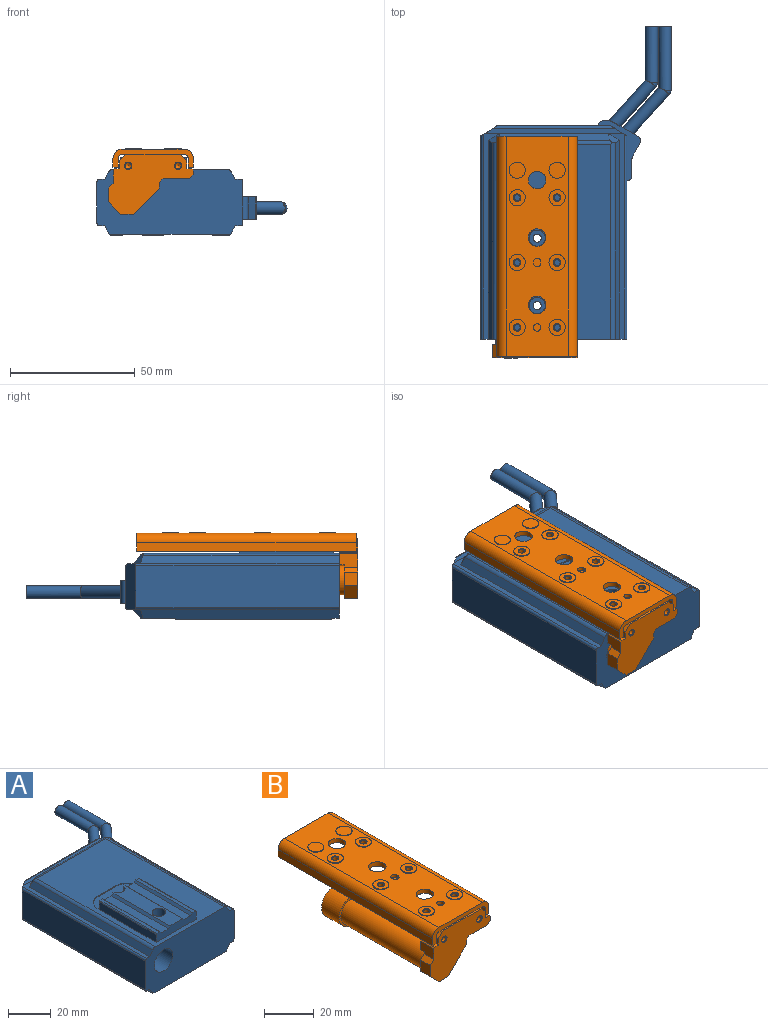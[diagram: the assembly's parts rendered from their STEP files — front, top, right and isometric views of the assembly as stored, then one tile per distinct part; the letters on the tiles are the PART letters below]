
ASSEMBLY  parts=2 mates=1
PART A: 108 faces, bbox 76.8x126.2x32.1 mm
  f0: plane 5x5mm, normal (0,1,0), area 19.6mm2, adj f3
  f1: plane 5x5mm, normal (0,1,0), area 19.6mm2, adj f4
  f2: revolved ~5x2.5mm, area 9.1mm2, adj f3,f8
  f3: cylinder r=2.5mm len=22.72mm, axis (0,1,0), area 353.2mm2, adj f0,f2,f8
  f4: cylinder r=2.5mm len=25.66mm, axis (0,-1,0), area 398.3mm2, adj f1,f5,f9
  f5: sphere r=2.5mm, area 11.9mm2, adj f4,f9
  f6: plane 6.5x6.5mm, normal (0,0,1), area 24.6mm2, adj f11,f13
  f7: plane 6.5x6.5mm, normal (0,0,1), area 24.6mm2, adj f10,f14
  f8: cylinder r=2.5mm len=20.28mm, axis (0.67,0.74,0), area 340.2mm2, adj f2,f3,f15,f17,f18,f19
  f9: cylinder r=2.5mm len=20.09mm, axis (-0.67,-0.74,0), area 340.4mm2, adj f4,f5,f19
  f10: cylinder r=3.25mm len=7.9mm, axis (0,0,1), area 161.3mm2, adj f7,f28
  f11: cylinder r=3.25mm len=7.9mm, axis (0,0,1), area 98.6mm2, adj f6,f28,f34,f35,f36
  f12: plane 14.2x14.2mm, normal (0,-1,0), area 158.4mm2, adj f38
  f13: cylinder r=1.65mm len=23.15mm, axis (0,0,1), area 240mm2, adj f6,f39
  f14: cylinder r=1.65mm len=23.15mm, axis (0,0,1), area 240mm2, adj f7,f40
  f15: cylinder r=2mm len=3.59mm, axis (0,0,-1), area 3.2mm2, adj f8,f17,f19,f44
  f16: cylinder r=2mm len=9mm, axis (0,0,-1), area 28.3mm2, adj f17,f43,f44,f45
  f17: plane 9.08x2.54mm, normal (0,1,0), area 21.9mm2, adj f8,f15,f16,f18,f44,f45
  f18: cylinder r=2mm len=3.59mm, axis (0,0,-1), area 3.2mm2, adj f8,f17,f19,f45
  f19: plane 10.72x9.22mm, normal (0.5,0.87,0), area 72.3mm2, adj f8,f9,f15,f18,f20,f44,f45
  f20: cylinder r=2mm len=9mm, axis (0,0,-1), area 28.3mm2, adj f19,f21,f44,f45
  f21: plane 9x5.07mm, normal (0.87,-0.5,0), area 52.7mm2, adj f20,f22,f44,f45
  f22: cylinder r=2mm len=9mm, axis (0,0,-1), area 9.4mm2, adj f21,f23,f44,f45
  f23: plane 9x6.86mm, normal (1,0,0), area 61.8mm2, adj f22,f44,f45,f46
  f24: plane 37.6x1.8mm, normal (0,0,1), area 67.7mm2, adj f25,f36,f37,f49
  f25: plane 37.6x1.1mm, normal (-0.71,0,0.71), area 58.5mm2, adj f24,f26,f36,f49
  f26: plane 37.6x4.6mm, normal (0,0,1), area 173mm2, adj f25,f27,f36,f49
  f27: plane 37.6x1.1mm, normal (0.71,0,0.71), area 58.5mm2, adj f26,f28,f36,f49
  f28: plane 37.6x8.2mm, normal (0,0,1), area 263.1mm2, adj f10,f11,f27,f29,f34,f36,f49
  f29: plane 37.6x1.1mm, normal (-0.71,0,0.71), area 58.5mm2, adj f28,f30,f34,f49
  f30: plane 37.6x4.6mm, normal (0,0,1), area 173mm2, adj f29,f31,f34,f49
  f31: plane 37.6x1.1mm, normal (0.71,0,0.71), area 58.5mm2, adj f30,f32,f34,f49
  f32: plane 37.6x1.8mm, normal (0,0,1), area 67.7mm2, adj f31,f33,f34,f49
  f33: cylinder r=0.5mm len=37.6mm, axis (0,-1,0), area 29.5mm2, adj f32,f34,f49,f50
  f34: plane 10.03x5.4mm, normal (0,1,0), area 47.8mm2, adj f11,f28,f29,f30,f31,f32,f33,f35
  f35: plane 26.4x8.2mm, normal (0,0,1), area 171.2mm2, adj f11,f34,f36,f51,f52,f53,f54,f55
  f36: plane 10.03x5.4mm, normal (0,1,0), area 47.8mm2, adj f11,f24,f25,f26,f27,f28,f35,f37
  f37: cylinder r=0.5mm len=37.6mm, axis (0,-1,0), area 29.5mm2, adj f24,f36,f49,f56
  f38: cylinder r=7.1mm len=42mm, axis (0,1,0), area 1873.6mm2, adj f12,f60
  f39: cone r=0mm half-angle=45deg, axis (0,0,-1), area 5.7mm2, adj f13,f62
  f40: cone r=0mm half-angle=45deg, axis (0,0,-1), area 5.7mm2, adj f14,f62
  f41: plane 55.15x2mm, normal (0,0,1), area 103.9mm2, adj f42,f47,f58,f64
  f42: cylinder r=1mm len=48.72mm, axis (-1,0,0), area 74mm2, adj f41,f43,f47,f64
  f43: plane 45.5x16.5mm, normal (0,1,0), area 705.8mm2, adj f16,f42,f44,f45,f47,f64,f65,f66
  f44: plane 24x16.97mm, normal (0,0,1), area 81mm2, adj f15,f16,f17,f19,f20,f21,f22,f23
  f45: plane 24x16.97mm, normal (0,0,-1), area 81mm2, adj f16,f17,f18,f19,f20,f21,f22,f23
  f46: cylinder r=2mm len=9mm, axis (0,0,-1), area 28.3mm2, adj f23,f44,f45,f69
  f47: plane 7.68x7.18mm, normal (0.53,0.85,0), area 52mm2, adj f41,f42,f43,f44,f58,f69,f70,f71
  f48: plane 4.87x4.18mm, normal (0.44,0.75,0.5), area 14.8mm2, adj f57,f58,f71,f72,f73
  f49: plane 26.4x4.9mm, normal (0,-1,0), area 116.7mm2, adj f24,f25,f26,f27,f28,f29,f30,f31
  f50: plane 37.6x4.4mm, normal (-1,0,0), area 165.4mm2, adj f33,f34,f49,f74
  f51: plane 0.7x0.5mm, normal (1,0,0), area 0.3mm2, adj f34,f35,f52,f74
  f52: cylinder r=7.5mm len=7.5mm, axis (0,0,1), area 5.9mm2, adj f35,f51,f53,f74
  f53: plane 11.4x0.5mm, normal (0,-1,0), area 5.7mm2, adj f35,f52,f54,f74
  f54: cylinder r=7.5mm len=7.5mm, axis (0,0,1), area 5.9mm2, adj f35,f53,f55,f74
  f55: plane 0.7x0.5mm, normal (-1,0,0), area 0.3mm2, adj f35,f36,f54,f74
  f56: plane 37.6x4.4mm, normal (1,0,0), area 165.4mm2, adj f36,f37,f49,f74
  f57: cylinder r=2mm len=46.85mm, axis (-1,0,0), area 80.7mm2, adj f48,f58,f59,f73,f74,f75
  f58: plane 55.56x3.43mm, normal (0,0.77,0.64), area 199.9mm2, adj f41,f47,f48,f57,f59,f64,f71,f77
  f59: plane 4.87x4.18mm, normal (-0.44,0.75,0.5), area 14.8mm2, adj f57,f58,f75,f76,f77
  f60: plane 14.2x14.2mm, normal (0,1,0), area 41.5mm2, adj f38,f81
  f61: plane 62.5x4.98mm, normal (0,0,-1), area 311.2mm2, adj f83,f84,f85,f86
  f62: plane 62.5x8.57mm, normal (0,0,-1), area 510.5mm2, adj f39,f40,f88,f89,f90,f91
  f63: plane 45.07x2.92mm, normal (0,0.74,-0.67), area 172.3mm2, adj f67,f82,f87,f92
  f64: plane 19.18x7.18mm, normal (-0.53,0.85,0), area 139.6mm2, adj f41,f42,f43,f58,f65,f77,f78,f79
  f65: cylinder r=1mm len=47.02mm, axis (-1,0,0), area 47mm2, adj f43,f64,f66,f93
  f66: plane 6.86x4.4mm, normal (0.53,0.85,0), area 18.7mm2, adj f43,f45,f65,f68,f69,f93
  f67: plane 42.9x0.42mm, normal (0,0.87,-0.5), area 20.7mm2, adj f63,f87,f92,f93
  f68: cylinder r=1mm len=82.08mm, axis (0,-1,0), area 128.4mm2, adj f66,f69,f93,f94
  f69: plane 81.46x16.5mm, normal (1,0,0), area 1182.4mm2, adj f44,f45,f46,f47,f66,f68,f70,f94
  f70: cylinder r=1mm len=82.08mm, axis (0,-1,0), area 128.4mm2, adj f47,f69,f71,f94
  f71: plane 82.38x6.59mm, normal (0,0,1), area 170.8mm2, adj f47,f48,f58,f70,f72,f94
  f72: plane 79.7x3mm, normal (0.87,0,0.5), area 274.4mm2, adj f48,f71,f73,f94
  f73: cylinder r=2mm len=78.74mm, axis (0,-1,0), area 164.7mm2, adj f48,f57,f72,f74,f94
  f74: plane 78.1x45.57mm, normal (0,0,1), area 2374.4mm2, adj f49,f50,f51,f52,f53,f54,f55,f56
  f75: cylinder r=2mm len=78.74mm, axis (0,-1,0), area 159.9mm2, adj f57,f59,f74,f76,f94
  f76: plane 79.7x3.05mm, normal (-0.87,0,0.5), area 279.1mm2, adj f59,f75,f77,f94
  f77: plane 82.38x6.59mm, normal (0,0,1), area 170.8mm2, adj f58,f59,f64,f76,f78,f94
  f78: cylinder r=1mm len=82.08mm, axis (0,-1,0), area 128.4mm2, adj f64,f77,f79,f94
  f79: plane 81.46x16.5mm, normal (-1,0,0), area 1344.1mm2, adj f64,f78,f80,f94
  f80: cylinder r=1mm len=82.08mm, axis (0,-1,0), area 128.4mm2, adj f64,f79,f93,f94
  f81: cylinder r=6.1mm len=12.5mm, axis (0,1,0), area 479.1mm2, adj f60,f94
  f82: cylinder r=2mm len=45.26mm, axis (-1,0,0), area 10.5mm2, adj f63,f87,f92,f95
  f83: plane 5.56x0.5mm, normal (0,-1,0), area 2.6mm2, adj f61,f84,f86,f95
  f84: plane 62.5x0.5mm, normal (0.87,0,-0.5), area 36.1mm2, adj f61,f83,f85,f95
  f85: plane 5.56x0.5mm, normal (0,1,0), area 2.6mm2, adj f61,f84,f86,f95
  f86: plane 79.7x4mm, normal (-0.87,0,-0.5), area 355.8mm2, adj f61,f83,f85,f87,f93,f94,f95
  f87: plane 4.88x3.97mm, normal (-0.44,0.75,-0.5), area 15.5mm2, adj f63,f67,f82,f86,f93,f95
  f88: plane 9.15x0.5mm, normal (0,1,0), area 4.4mm2, adj f62,f89,f91,f95
  f89: plane 62.5x0.5mm, normal (-0.87,0,-0.5), area 36.1mm2, adj f62,f88,f90,f95
  f90: plane 9.15x0.5mm, normal (0,-1,0), area 4.4mm2, adj f62,f89,f91,f95
  f91: plane 62.5x0.5mm, normal (0.87,0,-0.5), area 36.1mm2, adj f62,f88,f90,f95
  f92: plane 4.88x3.97mm, normal (0.44,0.75,-0.5), area 15.5mm2, adj f63,f67,f82,f93,f95,f98
  f93: plane 85.03x56.5mm, normal (0,0,-1), area 472.2mm2, adj f64,f65,f66,f67,f68,f80,f86,f87
  f94: plane 58.5x26mm, normal (0,-1,0), area 1341.5mm2, adj f68,f69,f70,f71,f72,f73,f74,f75
  f95: plane 79.47x48.46mm, normal (0,0,-1), area 2458.4mm2, adj f82,f83,f84,f85,f86,f87,f88,f89
  f96: plane 3x3mm, normal (0,0,-1), area 7.1mm2, adj f102
  f97: plane 7.56x0.5mm, normal (0,1,0), area 3.6mm2, adj f95,f98,f100,f105
  f98: plane 79.7x4mm, normal (0.87,0,-0.5), area 355.9mm2, adj f92,f93,f94,f95,f97,f99,f105
  f99: plane 7.56x0.5mm, normal (0,-1,0), area 3.6mm2, adj f95,f98,f100,f105
  f100: plane 62.5x0.5mm, normal (-0.87,0,-0.5), area 36.1mm2, adj f95,f97,f99,f105
  f101: plane 3x1mm, normal (1,0,0), area 3mm2, adj f103,f104,f105,f107
  f102: cylinder r=1.5mm len=3mm, axis (0,0,1), area 28.3mm2, adj f96,f105
  f103: cylinder r=1.5mm len=3mm, axis (0,0,-1), area 14.1mm2, adj f101,f104,f105,f106
  f104: plane 4x3mm, normal (0,0,-1), area 10.1mm2, adj f101,f103,f106,f107
  f105: plane 62.5x6.98mm, normal (0,0,-1), area 419.1mm2, adj f97,f98,f99,f100,f101,f102,f103,f106
  f106: plane 3x1mm, normal (-1,0,0), area 3mm2, adj f103,f104,f105,f107
  f107: cylinder r=1.5mm len=3mm, axis (0,0,-1), area 14.1mm2, adj f101,f104,f105,f106
PART B: 93 faces, bbox 34.1x88.7x26.4 mm
  f0: plane 14x14mm, normal (0,1,0), area 153.9mm2, adj f3
  f1: cone r=0mm half-angle=60deg, axis (0,-1,0), area 5.5mm2, adj f4
  f2: cone r=0mm half-angle=60deg, axis (0,-1,0), area 5.5mm2, adj f5
  f3: cylinder r=7mm len=14mm, axis (0,1,0), area 439.8mm2, adj f0,f6
  f4: cylinder r=1.23mm len=5.73mm, axis (0,-1,0), area 44.3mm2, adj f1,f12
  f5: cylinder r=1.23mm len=5.73mm, axis (0,-1,0), area 44.3mm2, adj f2,f13
  f6: plane 14x14mm, normal (0,-1,0), area 40.8mm2, adj f3,f14
  f7: plane 20x13.5mm, normal (0,1,0), area 64.5mm2, adj f8,f9,f10,f11,f14,f15,f16,f27
  f8: plane 5.5x2mm, normal (-0.71,0,0.71), area 15.6mm2, adj f7,f9,f16,f36
  f9: plane 5.5x5.5mm, normal (-1,0,0), area 30.2mm2, adj f7,f8,f10,f36
  f10: plane 5.5x5mm, normal (-0.71,0,-0.71), area 38.9mm2, adj f7,f9,f11,f36
  f11: plane 5.5x5mm, normal (0,0,-1), area 27.5mm2, adj f7,f10,f27,f36
  f12: cone r=0mm half-angle=45deg, axis (0,-1,0), area 3.3mm2, adj f4,f36
  f13: cone r=0mm half-angle=45deg, axis (0,-1,0), area 3.3mm2, adj f5,f36
  f14: cylinder r=6mm len=47mm, axis (0,1,0), area 1756.7mm2, adj f6,f7,f15,f28,f38
  f15: plane 2.94x2mm, normal (-0.19,0,-0.98), area 6mm2, adj f7,f14,f16,f38
  f16: plane 7.5x5.3mm, normal (-1,0,0), area 37.8mm2, adj f7,f8,f15,f17,f36,f38
  f17: plane 7.5x0.5mm, normal (-0.71,0,0.71), area 5.3mm2, adj f16,f18,f36,f38
  f18: plane 7.5x2mm, normal (0,0,1), area 15mm2, adj f17,f29,f36,f38
  f19: plane 7.5x3.2mm, normal (1,0,0), area 24mm2, adj f20,f36,f37,f38
  f20: plane 7.5x2mm, normal (0,0,1), area 15mm2, adj f19,f21,f36,f38
  f21: plane 7.5x0.5mm, normal (0.71,0,0.71), area 5.3mm2, adj f20,f22,f36,f38
  f22: plane 7.5x2mm, normal (1,0,0), area 15mm2, adj f21,f23,f36,f38
  f23: plane 7.5x1.5mm, normal (0.71,0,-0.71), area 15.9mm2, adj f22,f24,f36,f38
  f24: plane 10.5x7.5mm, normal (0,0,-1), area 78.8mm2, adj f23,f25,f36,f38
  f25: plane 7.5x1.5mm, normal (0.71,0,-0.71), area 15.9mm2, adj f24,f26,f36,f38
  f26: plane 7.5x2.3mm, normal (1,0,0), area 17.2mm2, adj f25,f27,f36,f38
  f27: plane 10.5x10.5mm, normal (0.71,0,-0.71), area 83.1mm2, adj f7,f11,f26,f28,f36,f38
  f28: plane 8.1x2mm, normal (-0.19,0,-0.98), area 16.5mm2, adj f7,f14,f27,f38
  f29: plane 7.5x3.2mm, normal (-1,0,0), area 24mm2, adj f18,f36,f38,f39
  f30: cylinder r=1.23mm len=2.46mm, axis (0,0,-1), area 14.4mm2, adj f40,f46
  f31: cylinder r=1.23mm len=2.46mm, axis (0,0,-1), area 14.4mm2, adj f41,f47
  f32: cylinder r=1.23mm len=2.46mm, axis (0,0,-1), area 14.4mm2, adj f42,f48
  f33: cylinder r=1.23mm len=2.46mm, axis (0,0,-1), area 14.4mm2, adj f43,f49
  f34: cylinder r=1.23mm len=2.46mm, axis (0,0,-1), area 14.4mm2, adj f44,f50
  f35: cylinder r=1.23mm len=2.46mm, axis (0,0,-1), area 14.4mm2, adj f45,f51
  f36: plane 34x24mm, normal (0,-1,0), area 481.2mm2, adj f8,f9,f10,f11,f12,f13,f16,f17
  f37: plane 7.5x2.5mm, normal (0.71,0,0.71), area 26.5mm2, adj f19,f36,f38,f56,f63
  f38: plane 32x14mm, normal (0,1,0), area 317.7mm2, adj f14,f15,f16,f17,f18,f19,f20,f21
  f39: plane 7.5x2.5mm, normal (-0.71,0,0.71), area 26.5mm2, adj f29,f36,f38,f56,f63
  f40: cone r=0mm half-angle=45deg, axis (0,0,-1), area 3.3mm2, adj f30,f63
  f41: cone r=0mm half-angle=45deg, axis (0,0,-1), area 3.3mm2, adj f31,f63
  f42: cone r=0mm half-angle=45deg, axis (0,0,-1), area 3.3mm2, adj f32,f63
  f43: cone r=0mm half-angle=45deg, axis (0,0,-1), area 3.3mm2, adj f33,f63
  f44: cone r=0mm half-angle=45deg, axis (0,0,-1), area 3.3mm2, adj f34,f63
  f45: cone r=0mm half-angle=45deg, axis (0,0,-1), area 3.3mm2, adj f35,f63
  f46: cone r=0mm half-angle=45deg, axis (0,0,1), area 3.3mm2, adj f30,f65
  f47: cone r=0mm half-angle=45deg, axis (0,0,1), area 3.3mm2, adj f31,f66
  f48: cone r=0mm half-angle=45deg, axis (0,0,1), area 3.3mm2, adj f32,f67
  f49: cone r=0mm half-angle=45deg, axis (0,0,1), area 3.3mm2, adj f33,f68
  f50: cone r=0mm half-angle=45deg, axis (0,0,1), area 3.3mm2, adj f34,f69
  f51: cone r=0mm half-angle=45deg, axis (0,0,1), area 3.3mm2, adj f35,f70
  f52: plane 88x3.6mm, normal (-1,0,0), area 316.8mm2, adj f53,f71,f72,f73
  f53: plane 88x2.1mm, normal (0,0,-1), area 184.8mm2, adj f52,f54,f71,f73
  f54: plane 88x3.6mm, normal (1,0,0), area 316.8mm2, adj f53,f55,f71,f73
  f55: cylinder r=1.6mm len=88mm, axis (0,1,0), area 221.2mm2, adj f54,f63,f71,f73
  f56: plane 22x0.7mm, normal (0,0,1), area 15.4mm2, adj f36,f37,f39,f73
  f57: cylinder r=1.6mm len=88mm, axis (0,1,0), area 221.2mm2, adj f58,f63,f71,f73
  f58: plane 88x3.6mm, normal (-1,0,0), area 316.8mm2, adj f57,f59,f71,f73
  f59: plane 88x2.1mm, normal (0,0,-1), area 184.8mm2, adj f58,f60,f71,f73
  f60: plane 88x3.6mm, normal (1,0,0), area 316.8mm2, adj f59,f71,f73,f74
  f61: plane 6.5x6.5mm, normal (0,0,1), area 33.2mm2, adj f75
  f62: plane 6.5x6.5mm, normal (0,0,1), area 33.2mm2, adj f76
  f63: plane 88x24.8mm, normal (0,0,-1), area 1874.9mm2, adj f37,f38,f39,f40,f41,f42,f43,f44
  f64: plane 3x3mm, normal (0,0,1), area 7.1mm2, adj f81
  f65: plane 6.5x6.5mm, normal (0,0,1), area 26.1mm2, adj f46,f82
  f66: plane 6.5x6.5mm, normal (0,0,1), area 26.1mm2, adj f47,f83
  f67: plane 6.5x6.5mm, normal (0,0,1), area 26.1mm2, adj f48,f84
  f68: plane 6.5x6.5mm, normal (0,0,1), area 26.1mm2, adj f49,f85
  f69: plane 6.5x6.5mm, normal (0,0,1), area 26.1mm2, adj f50,f86
  f70: plane 6.5x6.5mm, normal (0,0,1), area 26.1mm2, adj f51,f87
  f71: plane 32.2x7.3mm, normal (0,1,0), area 84.7mm2, adj f52,f53,f54,f55,f57,f58,f59,f60
  f72: cylinder r=3.7mm len=88mm, axis (0,1,0), area 511.5mm2, adj f52,f71,f73,f90
  f73: plane 32.2x7.3mm, normal (0,-1,0), area 84.7mm2, adj f52,f53,f54,f55,f56,f57,f58,f59
  f74: cylinder r=3.7mm len=88mm, axis (0,1,0), area 511.5mm2, adj f60,f71,f73,f90
  f75: cylinder r=3.25mm len=6.5mm, axis (0,0,-1), area 6.1mm2, adj f61,f90
  f76: cylinder r=3.25mm len=6.5mm, axis (0,0,-1), area 6.1mm2, adj f62,f90
  f77: cylinder r=3.5mm len=7mm, axis (0,0,1), area 46.2mm2, adj f63,f90
  f78: cylinder r=3.5mm len=7mm, axis (0,0,-1), area 46.2mm2, adj f63,f90
  f79: cylinder r=3.5mm len=7mm, axis (0,0,-1), area 46.2mm2, adj f63,f90
  f80: plane 1.5x0.5mm, normal (1,0,0), area 0.8mm2, adj f88,f89,f90,f92
  f81: cylinder r=1.5mm len=3mm, axis (0,0,1), area 14.1mm2, adj f64,f90
  f82: cylinder r=3.25mm len=6.5mm, axis (0,0,-1), area 6.1mm2, adj f65,f90
  f83: cylinder r=3.25mm len=6.5mm, axis (0,0,-1), area 6.1mm2, adj f66,f90
  f84: cylinder r=3.25mm len=6.5mm, axis (0,0,-1), area 6.1mm2, adj f67,f90
  f85: cylinder r=3.25mm len=6.5mm, axis (0,0,-1), area 6.1mm2, adj f68,f90
  f86: cylinder r=3.25mm len=6.5mm, axis (0,0,-1), area 6.1mm2, adj f69,f90
  f87: cylinder r=3.25mm len=6.5mm, axis (0,0,-1), area 6.1mm2, adj f70,f90
  f88: cylinder r=1.5mm len=3mm, axis (0,0,1), area 7.1mm2, adj f80,f89,f90,f91
  f89: plane 3.5x3mm, normal (0,0,1), area 8.6mm2, adj f80,f88,f91,f92
  f90: plane 88x24.8mm, normal (0,0,1), area 1785.8mm2, adj f71,f72,f73,f74,f75,f76,f77,f78
  f91: plane 1.5x0.5mm, normal (-1,0,0), area 0.8mm2, adj f88,f89,f90,f92
  f92: cylinder r=1.5mm len=3mm, axis (0,0,1), area 7.1mm2, adj f80,f89,f90,f91
PLACE A t=(0,-7.42,-12.06)mm
PLACE B t=(0,-5.92,-12.06)mm
MATE slider B.f3 <-> A.f38  axis (0,1,0) through (-10.5,56.58,3.94)mm
